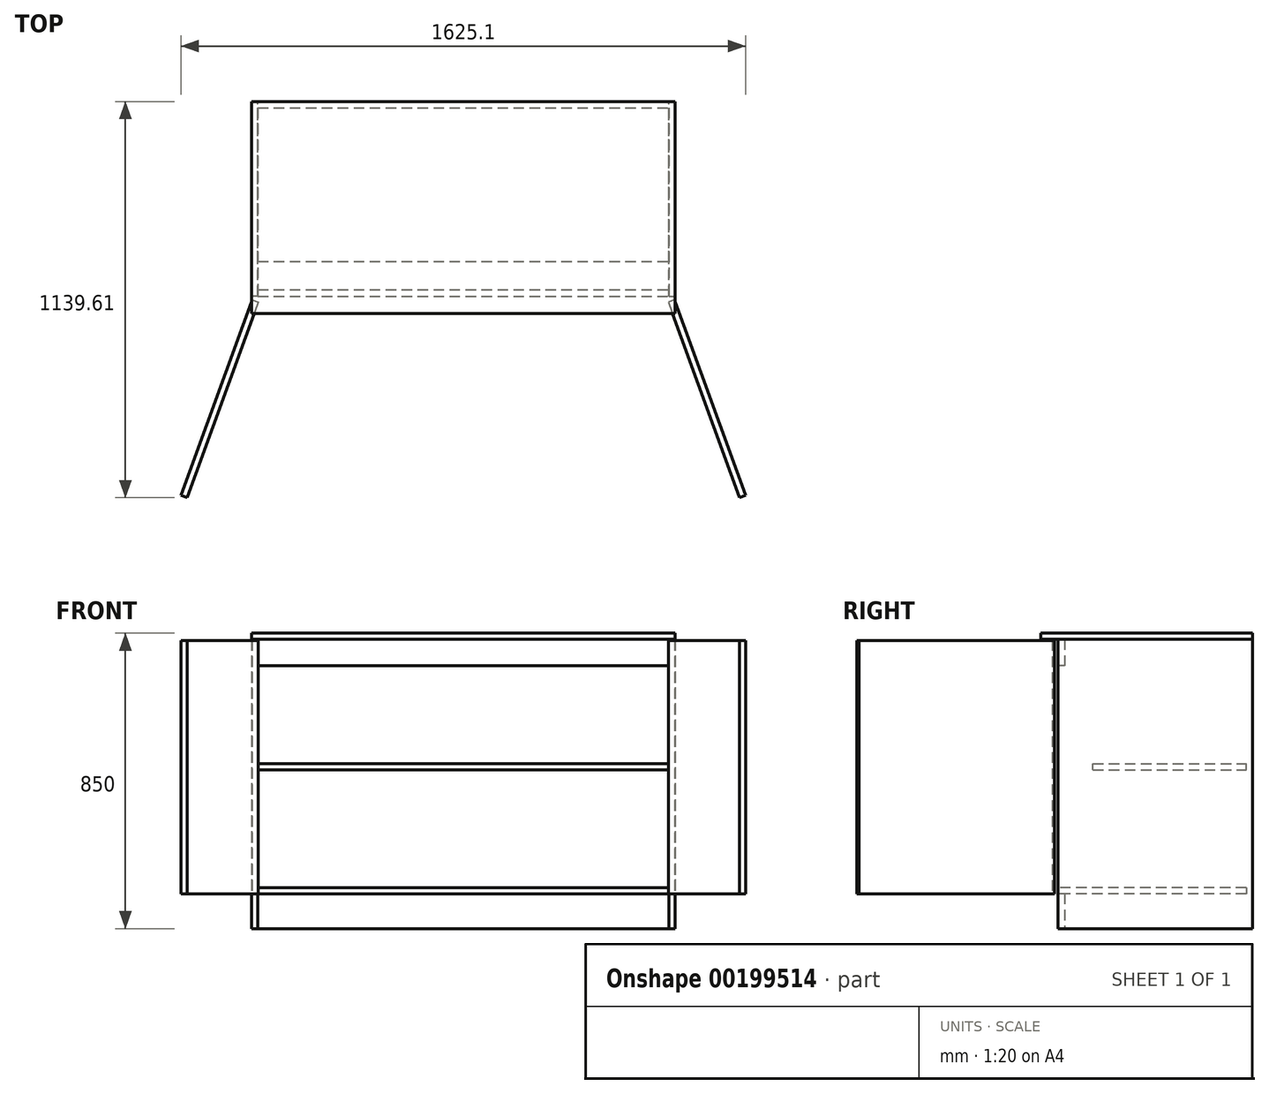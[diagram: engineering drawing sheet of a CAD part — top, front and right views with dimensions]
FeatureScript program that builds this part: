
annotation { "Feature Type Name" : "Feature", "Feature Type Description" : "" }
export const myFeature = defineFeature(function(context is Context, id is Id, definition is map)
    precondition{}
    {
        {
            var Q0;
            Q0=qCreatedBy(makeId("Top.planeOp"),FACE);
            cPlane(context, id + "F0", {"entities" : qUnion([Q0]), "cplaneType" : CPlaneType.OFFSET, "offset" : 850 * mm, "width" : 150 * mm, "height" : 150 * mm});
        }
        {
            var Q0;
            Q0=qCreatedBy(id+"F0.planeOp",FACE);
            var sketch = newSketch(context, id + "F1", { "sketchPlane" : qUnion([Q0])});
            skLineSegment(sketch, "E0.bottom", {"start": v(-609.6, -304.8) * mm, "end": v(609.6, -304.8) * mm});
            skLineSegment(sketch, "E0.top", {"start": v(-609.6, 304.8) * mm, "end": v(609.6, 304.8) * mm});
            skLineSegment(sketch, "E0.left", {"start": v(-609.6, -304.8) * mm, "end": v(-609.6, 304.8) * mm});
            skLineSegment(sketch, "E0.right", {"start": v(609.6, -304.8) * mm, "end": v(609.6, 304.8) * mm});
            skSolve(sketch);
        }
        {
            var Q0;
            Q0=qSketchRegion(id+"F1",true);
            extrude(context, id + "F2", {"entities" : qUnion([Q0]), "oppositeDirection" : true, "depth" : 18 * mm});
        }
        {
            var Q0;
            Q0=makeQuery(id+"F2.opExtrude","SWEPT_FACE",FACE,{"disambiguationData":[OSD([sQuery(id+"F1.wireOp",EDGE,"E0.right")])]});
            var sketch = newSketch(context, id + "F3", { "sketchPlane" : qUnion([Q0])});
            skLineSegment(sketch, "E1.bottom", {"start": v(304.8, 832) * mm, "end": v(-254.8, 832) * mm});
            skLineSegment(sketch, "E1.top", {"start": v(304.8, 0) * mm, "end": v(-254.8, 0) * mm});
            skLineSegment(sketch, "E1.left", {"start": v(304.8, 832) * mm, "end": v(304.8, 0) * mm});
            skLineSegment(sketch, "E1.right", {"start": v(-254.8, 832) * mm, "end": v(-254.8, 0) * mm});
            skSolve(sketch);
        }
        {
            var Q0;
            Q0=qSketchRegion(id+"F3",true);
            extrude(context, id + "F4", {"entities" : qUnion([Q0]), "oppositeDirection" : true, "depth" : 18 * mm});
        }
        {
            var Q0;
            Q0=makeQuery(id+"F4.opExtrude","SWEPT_BODY",BODY,{"disambiguationData":[OSD([sQuery(id+"F3.wireOp",EDGE,"E1.bottom"),sQuery(id+"F3.wireOp",EDGE,"E1.top"),sQuery(id+"F3.wireOp",EDGE,"E1.left"),sQuery(id+"F3.wireOp",EDGE,"E1.right")])]});
            var Q1;
            Q1=qCreatedBy(makeId("Right.planeOp"),FACE);
            mirror(context, id + "F5", {"entities" : qUnion([Q0]), "mirrorPlane" : qUnion([Q1])});
        }
        {
            var Q0;
            Q0=makeQuery(id+"F2.opExtrude","SWEPT_FACE",FACE,{"disambiguationData":[OSD([sQuery(id+"F1.wireOp",EDGE,"E0.top")])]});
            var sketch = newSketch(context, id + "F6", { "sketchPlane" : qUnion([Q0])});
            skLineSegment(sketch, "E2.top", {"start": v(-591.6, 0) * mm, "end": v(591.6, 0) * mm});
            skLineSegment(sketch, "E2.left", {"start": v(-591.6, 832) * mm, "end": v(-591.6, 0) * mm});
            skLineSegment(sketch, "E2.right", {"start": v(591.6, 832) * mm, "end": v(591.6, 0) * mm});
            skLineSegment(sketch, "E3.bottom", {"start": v(-609.6, 832) * mm, "end": v(-591.6, 832) * mm});
            skLineSegment(sketch, "E3.top", {"start": v(-609.6, 1782) * mm, "end": v(609.6, 1782) * mm});
            skLineSegment(sketch, "E3.left", {"start": v(-609.6, 832) * mm, "end": v(-609.6, 1782) * mm});
            skLineSegment(sketch, "E3.right", {"start": v(609.6, 832) * mm, "end": v(609.6, 1782) * mm});
            skLineSegment(sketch, "E4.trimOffspring", {"start": v(591.6, 832) * mm, "end": v(609.6, 832) * mm});
            skSolve(sketch);
        }
        {
            var Q0;
            Q0=qSketchRegion(id+"F6",true);
            extrude(context, id + "F7", {"entities" : qUnion([Q0]), "oppositeDirection" : true, "depth" : 18 * mm});
        }
        {
            var Q0;
            Q0=makeQuery(id+"F5.opPattern","COPY",FACE,{"derivedFrom":makeQuery(id+"F4.opExtrude","SWEPT_FACE",FACE,{"disambiguationData":[OSD([sQuery(id+"F3.wireOp",EDGE,"E1.right")])]}),"instanceName":"1"});
            var sketch = newSketch(context, id + "F8", { "sketchPlane" : qUnion([Q0])});
            skLineSegment(sketch, "E5.bottom", {"start": v(-591.6, 832) * mm, "end": v(591.6, 832) * mm});
            skLineSegment(sketch, "E5.top", {"start": v(-591.6, 757) * mm, "end": v(591.6, 757) * mm});
            skLineSegment(sketch, "E5.left", {"start": v(-591.6, 832) * mm, "end": v(-591.6, 757) * mm});
            skLineSegment(sketch, "E5.right", {"start": v(591.6, 832) * mm, "end": v(591.6, 757) * mm});
            skLineSegment(sketch, "E6.bottom", {"start": v(-591.6, 0) * mm, "end": v(591.6, 0) * mm});
            skLineSegment(sketch, "E6.top", {"start": v(-591.6, 100) * mm, "end": v(591.6, 100) * mm});
            skLineSegment(sketch, "E6.left", {"start": v(-591.6, 100) * mm, "end": v(-591.6, 0) * mm});
            skLineSegment(sketch, "E6.right", {"start": v(591.6, 100) * mm, "end": v(591.6, 0) * mm});
            skLineSegment(sketch, "E7.top", {"start": v(-591.6, 118) * mm, "end": v(591.6, 118) * mm});
            skLineSegment(sketch, "E7.left", {"start": v(-591.6, 100) * mm, "end": v(-591.6, 118) * mm});
            skLineSegment(sketch, "E7.right", {"start": v(591.6, 100) * mm, "end": v(591.6, 118) * mm});
            skSolve(sketch);
        }
        {
            var Q0;
            Q0=makeQuery(id+"F8.imprint","IMPRINT",FACE,{"disambiguationData":[TD([[makeQuery(id+"F8.imprint","IMPRINT",EDGE,{"derivedFrom":sQuery(id+"F8.wireOp",EDGE,"E5.bottom")}),-1.0]])]});
            extrude(context, id + "F9", {"entities" : qUnion([Q0]), "oppositeDirection" : true, "depth" : 18 * mm});
        }
        {
            var Q0;
            Q0=makeQuery(id+"F8.imprint","IMPRINT",FACE,{"disambiguationData":[TD([[makeQuery(id+"F8.imprint","IMPRINT",EDGE,{"derivedFrom":sQuery(id+"F8.wireOp",EDGE,"E6.bottom")}),1.0]])]});
            extrude(context, id + "F10", {"entities" : qUnion([Q0]), "oppositeDirection" : true, "depth" : 18 * mm});
        }
        {
            var Q0;
            Q0=makeQuery(id+"F8.imprint","IMPRINT",FACE,{"disambiguationData":[TD([[makeQuery(id+"F8.imprint","IMPRINT",EDGE,{"derivedFrom":sQuery(id+"F8.wireOp",EDGE,"E6.top")}),1.0]])]});
            extrude(context, id + "F11", {"entities" : qUnion([Q0]), "endBound" : BoundingType.UP_TO_NEXT, "oppositeDirection" : true, "depth" : 25 * mm});
        }
        {
            var Q0;
            Q0=makeQuery(id+"F7.opExtrude","SWEPT_FACE",FACE,{"disambiguationData":[OSD([sQuery(id+"F6.wireOp",EDGE,"E3.left")])]});
            var sketch = newSketch(context, id + "F12", { "sketchPlane" : qUnion([Q0])});
            skLineSegment(sketch, "E8.bottom", {"start": v(304.8, 1782) * mm, "end": v(247.8, 1782) * mm});
            skLineSegment(sketch, "E8.top", {"start": v(304.8, 1800) * mm, "end": v(229.8, 1800) * mm});
            skLineSegment(sketch, "E8.left", {"start": v(304.8, 1782) * mm, "end": v(304.8, 1800) * mm});
            skLineSegment(sketch, "E8.right", {"start": v(229.8, 1782) * mm, "end": v(229.8, 1800) * mm});
            skLineSegment(sketch, "E9.top", {"start": v(229.8, 1760) * mm, "end": v(247.8, 1760) * mm});
            skLineSegment(sketch, "E9.left", {"start": v(229.8, 1782) * mm, "end": v(229.8, 1760) * mm});
            skLineSegment(sketch, "E9.right", {"start": v(247.8, 1782) * mm, "end": v(247.8, 1760) * mm});
            skSolve(sketch);
        }
        {
            var Q0;
            Q0=qSketchRegion(id+"F12",true);
            var Q1;
            Q1=makeQuery(id+"F7.opExtrude","SWEPT_FACE",FACE,{"disambiguationData":[OSD([sQuery(id+"F6.wireOp",EDGE,"E3.right")])]});
            extrude(context, id + "F13", {"entities" : qUnion([Q0]), "operationType" : NewBodyOperationType.ADD, "endBound" : BoundingType.UP_TO_SURFACE, "oppositeDirection" : true, "endBoundEntityFace" : qUnion([Q1]), "depth" : 25 * mm});
        }
        {
            var Q0;
            Q0=makeQuery(id+"F11.opExtrude","SWEPT_FACE",FACE,{"disambiguationData":[OSD([sQuery(id+"F8.wireOp",EDGE,"E7.top")])]});
            var Q1;
            Q1=makeQuery(id+"F2.opExtrude","CAP_FACE",FACE,{"disambiguationData":[OSD([sQuery(id+"F1.wireOp",EDGE,"E0.bottom"),sQuery(id+"F1.wireOp",EDGE,"E0.top"),sQuery(id+"F1.wireOp",EDGE,"E0.left"),sQuery(id+"F1.wireOp",EDGE,"E0.right")])],"isStart":false});
            cPlane(context, id + "F14", {"entities" : qUnion([Q0, Q1]), "cplaneType" : CPlaneType.MID_PLANE, "offset" : 25 * mm, "width" : 150 * mm, "height" : 150 * mm});
        }
        {
            var Q0;
            Q0=qCreatedBy(id+"F14.planeOp",FACE);
            var sketch = newSketch(context, id + "F15", { "sketchPlane" : qUnion([Q0])});
            skLineSegment(sketch, "E10.bottom", {"start": v(-591.6, -154.8) * mm, "end": v(591.6, -154.8) * mm});
            skLineSegment(sketch, "E10.top", {"start": v(-591.6, 286.8) * mm, "end": v(591.6, 286.8) * mm});
            skLineSegment(sketch, "E10.left", {"start": v(-591.6, -154.8) * mm, "end": v(-591.6, 286.8) * mm});
            skLineSegment(sketch, "E10.right", {"start": v(591.6, -154.8) * mm, "end": v(591.6, 286.8) * mm});
            skSolve(sketch);
        }
        {
            var Q0;
            Q0=qSketchRegion(id+"F15",true);
            extrude(context, id + "F16", {"entities" : qUnion([Q0]), "oppositeDirection" : true, "depth" : 18 * mm});
        }
        {
            var Q0;
            Q0=makeQuery(id+"F11.opExtrude","SWEPT_FACE",FACE,{"disambiguationData":[OSD([sQuery(id+"F8.wireOp",EDGE,"E7.top")])]});
            var sketch = newSketch(context, id + "F17", { "sketchPlane" : qUnion([Q0])});
            skLineSegment(sketch, "E11", {"start": v(591.6, -276.8) * mm, "end": v(680.19, -520.2) * mm});
            skSolve(sketch);
        }
        {
            var Q0;
            Q0=sQuery(id+"F17.wireOp",EDGE,"E11");
            cPlane(context, id + "F18", {"entities" : qUnion([Q0]), "cplaneType" : CPlaneType.LINE_ANGLE, "offset" : 25 * mm, "angle" : 90 * degree, "width" : 150 * mm, "height" : 150 * mm});
        }
        {
            var Q0;
            Q0=qCreatedBy(id+"F18.planeOp",FACE);
            var sketch = newSketch(context, id + "F19", { "sketchPlane" : qUnion([Q0])});
            skLineSegment(sketch, "E12.bottom", {"start": v(-457.77, 829) * mm, "end": v(-1056.27, 829) * mm});
            skLineSegment(sketch, "E12.top", {"start": v(-457.77, 100) * mm, "end": v(-1056.27, 100) * mm});
            skLineSegment(sketch, "E12.left", {"start": v(-457.77, 829) * mm, "end": v(-457.77, 100) * mm});
            skLineSegment(sketch, "E12.right", {"start": v(-1056.27, 829) * mm, "end": v(-1056.27, 100) * mm});
            skSolve(sketch);
        }
        {
            var Q0;
            Q0=qSketchRegion(id+"F19",true);
            extrude(context, id + "F20", {"entities" : qUnion([Q0]), "depth" : 19 * mm});
        }
        {
            var Q0;
            Q0=makeQuery(id+"F20.opExtrude","SWEPT_BODY",BODY,{"disambiguationData":[OSD([sQuery(id+"F19.wireOp",EDGE,"E12.bottom"),sQuery(id+"F19.wireOp",EDGE,"E12.top"),sQuery(id+"F19.wireOp",EDGE,"E12.left"),sQuery(id+"F19.wireOp",EDGE,"E12.right")])]});
            var Q1;
            Q1=qCreatedBy(makeId("Right.planeOp"),FACE);
            mirror(context, id + "F21", {"entities" : qUnion([Q0]), "mirrorPlane" : qUnion([Q1])});
        }
        {
            var Q0;
            Q0=makeQuery(id+"F7.opExtrude","SWEPT_BODY",BODY,{"disambiguationData":[OSD([sQuery(id+"F6.wireOp",EDGE,"E2.top"),sQuery(id+"F6.wireOp",EDGE,"E2.left"),sQuery(id+"F6.wireOp",EDGE,"E2.right"),sQuery(id+"F6.wireOp",EDGE,"E3.bottom"),sQuery(id+"F6.wireOp",EDGE,"E3.top"),sQuery(id+"F6.wireOp",EDGE,"E3.left"),sQuery(id+"F6.wireOp",EDGE,"E3.right"),sQuery(id+"F6.wireOp",EDGE,"E4.trimOffspring")])]});
            deleteBodies(context, id + "F22", {"entities" : qUnion([Q0])});
        }
    });
